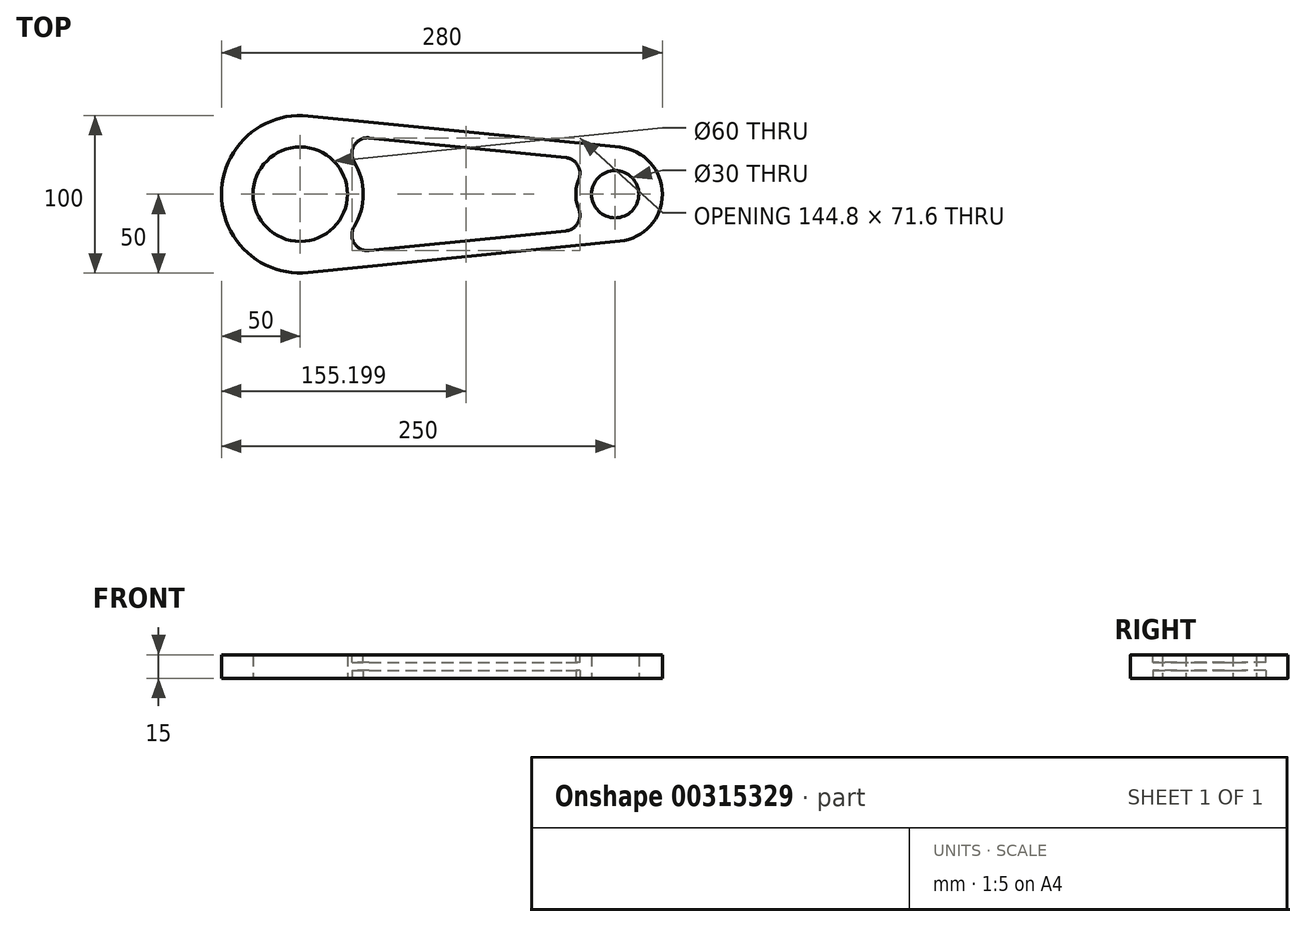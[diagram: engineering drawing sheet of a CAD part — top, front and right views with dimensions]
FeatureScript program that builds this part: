
annotation { "Feature Type Name" : "Feature", "Feature Type Description" : "" }
export const myFeature = defineFeature(function(context is Context, id is Id, definition is map)
    precondition{}
    {
        {
            var Q0;
            Q0=qCreatedBy(makeId("Top.planeOp"),FACE);
            var sketch = newSketch(context, id + "F0", { "sketchPlane" : qUnion([Q0])});
            skArc(sketch, "E0", {"start": v(5, 49.75) * mm, "mid": v(-50, 0) * mm, "end": v(5, -49.75) * mm});
            skArc(sketch, "E1", {"start": v(203, -29.85) * mm, "mid": v(230, 0) * mm, "end": v(203, 29.85) * mm});
            skLineSegment(sketch, "E2", {"start": v(5, 49.75) * mm, "end": v(203, 29.85) * mm});
            skLineSegment(sketch, "E3", {"start": v(5, -49.75) * mm, "end": v(203, -29.85) * mm});
            skSolve(sketch);
        }
        {
            var Q0;
            Q0=makeQuery(id+"F0.imprint","IMPRINT",FACE,{"disambiguationData":[TD([[makeQuery(id+"F0.imprint","IMPRINT",EDGE,{"derivedFrom":sQuery(id+"F0.wireOp",EDGE,"E0")}),1.0]])]});
            extrude(context, id + "F1", {"entities" : qUnion([Q0]), "depth" : 15 * mm});
        }
        {
            var Q0;
            Q0=qCreatedBy(makeId("Top.planeOp"),FACE);
            var sketch = newSketch(context, id + "F2", { "sketchPlane" : qUnion([Q0])});
            skPoint(sketch, "E4", {"position": v(0, 0) * mm});
            skPoint(sketch, "E5", {"position": v(200, 0) * mm});
            skSolve(sketch);
        }
        {
            var Q0;
            Q0=sQuery(id+"F2.wireOp",VERTEX,"E4");
            var Q1;
            Q1=makeQuery(id+"F1.opExtrude","SWEPT_BODY",BODY,{"disambiguationData":[OSD([sQuery(id+"F0.wireOp",EDGE,"E0"),sQuery(id+"F0.wireOp",EDGE,"E1"),sQuery(id+"F0.wireOp",EDGE,"E2"),sQuery(id+"F0.wireOp",EDGE,"E3")])]});
            hole(context, id + "F3", {"style" : HoleStyle.SIMPLE, "endStyle" : HoleEndStyle.THROUGH, "oppositeDirection" : true, "holeDiameter" : 60 * mm, "majorDiameter" : 5 * mm, "tappedDepth" : 12 * mm, "tapClearance" : 3, "locations" : qUnion([Q0]), "scope" : qUnion([Q1])});
        }
        {
            var Q0;
            Q0=sQuery(id+"F2.wireOp",VERTEX,"E5");
            var Q1;
            Q1=makeQuery(id+"F1.opExtrude","SWEPT_BODY",BODY,{"disambiguationData":[OSD([sQuery(id+"F0.wireOp",EDGE,"E0"),sQuery(id+"F0.wireOp",EDGE,"E1"),sQuery(id+"F0.wireOp",EDGE,"E2"),sQuery(id+"F0.wireOp",EDGE,"E3")])]});
            hole(context, id + "F4", {"style" : HoleStyle.SIMPLE, "endStyle" : HoleEndStyle.THROUGH, "oppositeDirection" : true, "holeDiameter" : 30 * mm, "tappedDepth" : 12 * mm, "tapClearance" : 3, "locations" : qUnion([Q0]), "scope" : qUnion([Q1])});
        }
        {
            var Q0;
            Q0=makeQuery(id+"F1.opExtrude","CAP_FACE",FACE,{"disambiguationData":[OSD([sQuery(id+"F0.wireOp",EDGE,"E0"),sQuery(id+"F0.wireOp",EDGE,"E1"),sQuery(id+"F0.wireOp",EDGE,"E2"),sQuery(id+"F0.wireOp",EDGE,"E3")])],"isStart":false});
            var sketch = newSketch(context, id + "F5", { "sketchPlane" : qUnion([Q0])});
            skLineSegment(sketch, "E6.0", {"start": v(43.8, 35.8) * mm, "end": v(168.63, 23.25) * mm});
            skLineSegment(sketch, "E7.0", {"start": v(43.8, -35.8) * mm, "end": v(168.63, -23.25) * mm});
            skArc(sketch, "E8.0", {"start": v(34.24, -20.68) * mm, "mid": v(40, 0) * mm, "end": v(34.24, 20.68) * mm});
            skArc(sketch, "E9.0", {"start": v(176.88, 9.5) * mm, "mid": v(175, 0) * mm, "end": v(176.88, -9.5) * mm});
            skPoint(sketch, "E10.visualSharp", {"position": v(4, 39.8) * mm});
            skArc(sketch, "E10.filletArc", {"start": v(43.8, 35.8) * mm, "mid": v(34.35, 31.2) * mm, "end": v(34.24, 20.68) * mm});
            skPoint(sketch, "E11.visualSharp", {"position": v(4, -39.8) * mm});
            skArc(sketch, "E11.filletArc", {"start": v(34.24, -20.68) * mm, "mid": v(34.35, -31.2) * mm, "end": v(43.8, -35.8) * mm});
            skPoint(sketch, "E12.visualSharp", {"position": v(187.08, 21.4) * mm});
            skArc(sketch, "E12.filletArc", {"start": v(176.88, 9.5) * mm, "mid": v(176.2, 18.45) * mm, "end": v(168.63, 23.25) * mm});
            skPoint(sketch, "E13.visualSharp", {"position": v(187.08, -21.4) * mm});
            skArc(sketch, "E13.filletArc", {"start": v(168.63, -23.25) * mm, "mid": v(176.2, -18.45) * mm, "end": v(176.88, -9.5) * mm});
            skSolve(sketch);
        }
        {
            var Q0;
            Q0 = qSketchRegion(id + "F5", true);
            extrude(context, id + "F6", {"entities" : qUnion([Q0]), "operationType" : NewBodyOperationType.REMOVE, "oppositeDirection" : true, "depth" : 5 * mm});
        }
        {
            var Q0;
            Q0=qCreatedBy(makeId("Top.planeOp"),FACE);
            var sketch = newSketch(context, id + "F7", { "sketchPlane" : qUnion([Q0])});
            skLineSegment(sketch, "E14.0", {"start": v(43.8, 35.8) * mm, "end": v(168.63, 23.25) * mm});
            skLineSegment(sketch, "E15.0", {"start": v(43.8, -35.8) * mm, "end": v(168.63, -23.25) * mm});
            skArc(sketch, "E16.0", {"start": v(34.24, -20.68) * mm, "mid": v(40, 0) * mm, "end": v(34.24, 20.68) * mm});
            skArc(sketch, "E17.0", {"start": v(176.88, 9.5) * mm, "mid": v(175, 0) * mm, "end": v(176.88, -9.5) * mm});
            skPoint(sketch, "E18.visualSharp", {"position": v(4, 39.8) * mm});
            skArc(sketch, "E18.filletArc", {"start": v(43.8, 35.8) * mm, "mid": v(34.35, 31.2) * mm, "end": v(34.24, 20.68) * mm});
            skPoint(sketch, "E19.visualSharp", {"position": v(4, -39.8) * mm});
            skArc(sketch, "E19.filletArc", {"start": v(34.24, -20.68) * mm, "mid": v(34.35, -31.2) * mm, "end": v(43.8, -35.8) * mm});
            skPoint(sketch, "E20.visualSharp", {"position": v(187.08, 21.4) * mm});
            skArc(sketch, "E20.filletArc", {"start": v(176.88, 9.5) * mm, "mid": v(176.2, 18.45) * mm, "end": v(168.63, 23.25) * mm});
            skPoint(sketch, "E21.visualSharp", {"position": v(187.08, -21.4) * mm});
            skArc(sketch, "E21.filletArc", {"start": v(168.63, -23.25) * mm, "mid": v(176.2, -18.45) * mm, "end": v(176.88, -9.5) * mm});
            skSolve(sketch);
        }
        {
            var Q0;
            Q0 = qSketchRegion(id + "F7", true);
            extrude(context, id + "F8", {"entities" : qUnion([Q0]), "operationType" : NewBodyOperationType.REMOVE, "depth" : 5 * mm});
        }
    });
